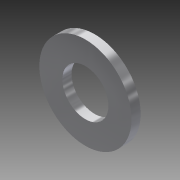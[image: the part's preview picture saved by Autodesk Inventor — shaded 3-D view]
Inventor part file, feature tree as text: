
AUTODESK INVENTOR PART (.ipt)
format: ipt  version: 2014 SP1 (Build 180222100, 222)  size: 79,360 bytes
history: native  units: in
note: dims shown in document units (in); Inventor stores cm internally (conversion verified against a paired STEP export)
features: extrude x1, sketch x1
ambient origin geometry x8: Origin, YZ Plane, XZ Plane, XY Plane, X Axis, Y Axis, Z Axis, Center Point
bodies: Solid1 (feature_tree)
feature tree (2):
  extrude  "Extrusion1"  Depth=0.3937in
  sketch  "Sketch1"  dims[d0=0.1969in d1=0.3937in d2=0.0394in d3=0.0in]
